# Revit family: Módulo para maniobras_Aguilera Electronica
name_source: partatom
category: Dispositivos de alarma de incendios
revit_build: Autodesk Revit 2017 (Build: 20160225_1515(x64)
units: mm (PartAtom-declared; Revit-internal decimal feet)

## family parameters
Anfitrión = Cara
Compartido = No
Corte con vacíos al cargar = No
Cota de conector redondo = Diámetro de uso
Mantener orientación de anotación = Sí
Número OmniClass = 23.85.30.21
Punto de cálculo de habitación = No
Tipo de pieza = Normal
Título OmniClass = Environmental Detection/Registration

## types (4) — shared parameters
Diámetro tubo = 20 mm  [stored 0.0656168 ft]
Elevación por defecto = 1200 mm
Fabricante = Aguilera Electrónica
Símbolo = Sí
Símbolo texto modelo = Sí
URL = http://aguilera.es

## per-type parameters (varying)
| type | Comentarios de tipo | Descripción | Modelo |
| Módulo de 2 salidas para maniobras |  | Unidad microprocesada direccionable fabricada por AGUILERA ELECTRÓNICA según norma EN 54-18, que gestiona dos salidas por relé libres de tensión: contactos NC (contactos cerrados) y NA (contactos abiertos y común) Especial para ejecutar dos maniobras independientes (cerrar puertas cortafuegos, activar o desactivar electroválvulas, etc.).
• Provisto de autoaislador que le aísla del resto de la instalación en caso de cortocircuito en su interior.
• Conexión a 2 hilos con clemas extraíbles.
• Alimentación: entre 18 y 27 Vcc.
• Consumo reposo/alarma: 2.6 mA.
• Montado en caja de ABS de 105 x 82 x 25mm. | AE/SA-2S |
| Módulo de 2 salidas vigiladas para maniobras |  | Unidad microprocesada direccionable fabricada por AGUILERA ELECTRÓNICA según norma EN 54-18, que gestiona dos salidas supervisadas de relé. Especial para ejecutar dos maniobras de evacuación independientes (sirenas, campanas, etc) según y para qué hayan sido configuradas desde la central en cumplimiento de la norma de instalación EN 54-14.
• Provisto de autoaislador que le aisla del resto de la instalación en caso de cortocircuito en su interior.
• Admite alimentación auxiliar para maniobras.
• Conexión a 2 hilos con clemas extraíbles.
• Alimentación: entre 18 y 27 Vcc.
• Consumo reposo 1 mA.
• Consumo máximo bucle alimentación auxiliar: 27 mA.
• Montado en caja de ABS de 105 x 82 x 25mm. | AE/SA-2SV |
| Módulo 1 salida y entrada que confirma maniobra |  | Unidad microprocesada direccionable fabricada por AGUILERA ELECTRÓNICA según norma EN 54-18 que gestiona una salida con relé libre de tensión para activar una maniobra y una entrada que confirma que ésta se ha realizado. Si la maniobra no fuese confirmada en un tiempo programado, la central indicará en su presentación esta situación. Especial para actuar sobre control de válvulas, compuertas y puertas cortafuegos cuando se quiere tener confirmación de que la maniobra se ha realizado.
• Provisto de autoaislador que le aísla del resto de la instalación en caso de cortocircuito en su interior.
• Conexión a 2 hilos con clemas extraíbles.
• Alimentación: entre 18 y 27 Vcc.
• Consumo reposo/alarma: 1.5 mA.
• Montado en ca ja de ABS de 105 x 82 x 25mm. | AE/SA-SE |
| Módulo 1 salida y entrada que confirma maniobra 230Vca | Para maniobras a 230Vca | Unidad microprocesada direccionable fabricada por AGUILERA ELECTRÓNICA según norma EN 54-18 que gestiona una salida con relé libre de tensión para activar una maniobra y una entrada que confirma que ésta se ha realizado. Si la maniobra no fuese confirmada en un tiempo programado, la central indicará en su presentación esta situación. Especial para actuar sobre control de válvulas, compuertas y puertas cortafuegos cuando se quiere tener confirmación de que la maniobra se ha realizado.
• Provisto de autoaislador que le aísla del resto de la instalación en caso de cortocircuito en su interior.
• Conexión a 2 hilos con clemas extraíbles.
• Alimentación: entre 18 y 27 Vcc.
• Consumo reposo/alarma: 1.5 mA.
• Montado en ca ja de ABS de 105 x 82 x 25mm. | AE/SA-SE230 |

note: [stored X ft] marks values corroborated as IEEE doubles in the binary element streams (Revit-internal decimal feet)
